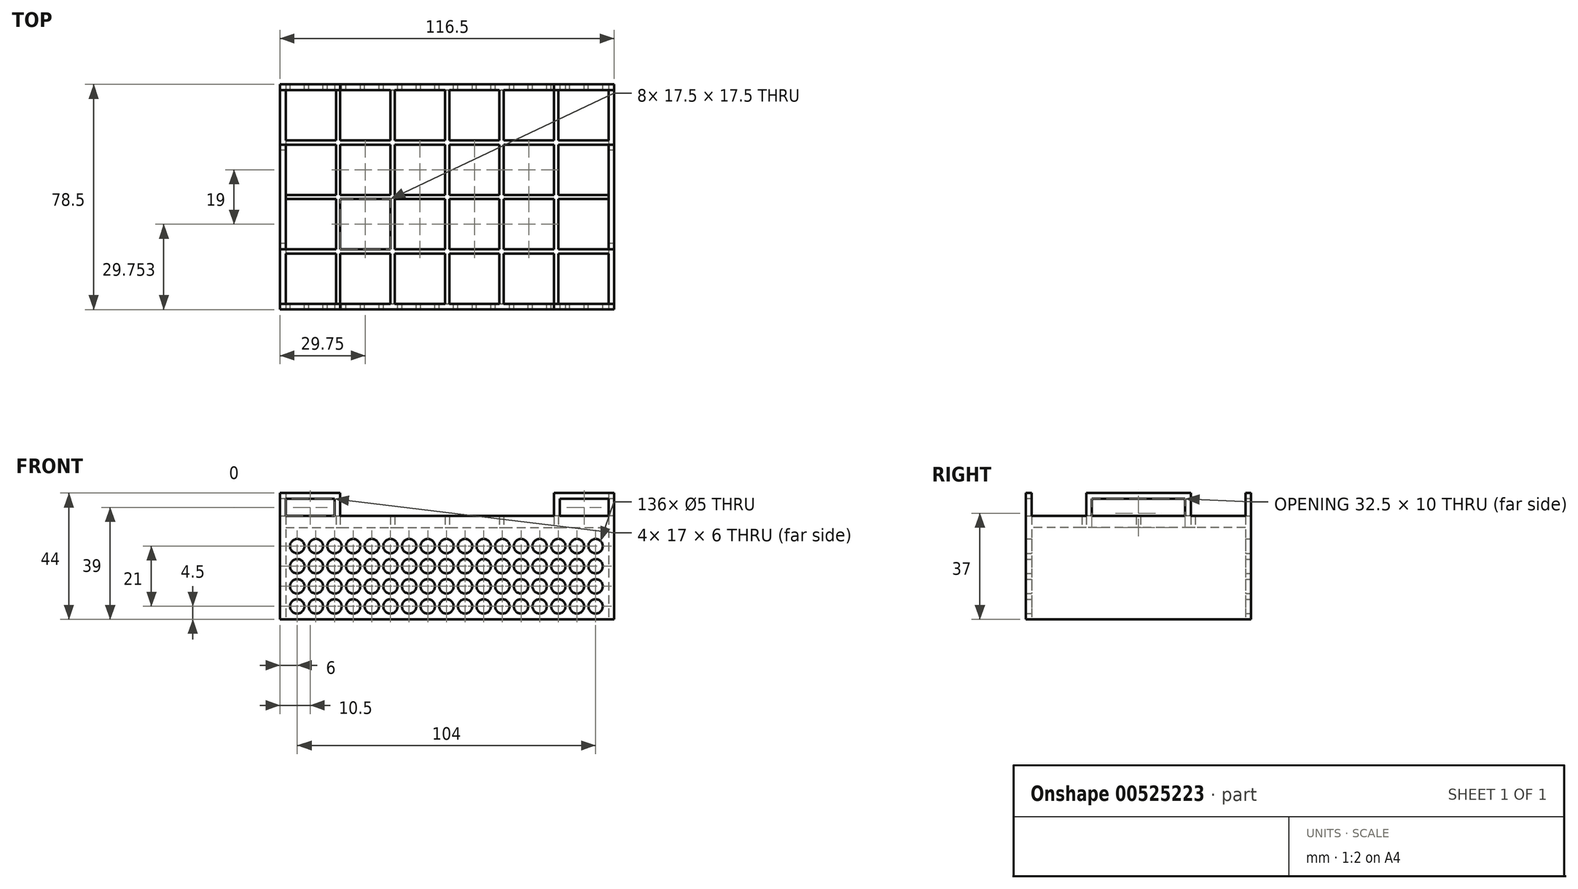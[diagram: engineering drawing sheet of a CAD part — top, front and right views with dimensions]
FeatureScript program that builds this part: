
annotation { "Feature Type Name" : "Feature", "Feature Type Description" : "" }
export const myFeature = defineFeature(function(context is Context, id is Id, definition is map)
    precondition{}
    {
        {
            var Q0;
            Q0=qCreatedBy(makeId("Top.planeOp"),FACE);
            var sketch = newSketch(context, id + "F0", { "sketchPlane" : qUnion([Q0])});
            skLineSegment(sketch, "E0.bottom", {"start": v(-60.16, 39.34) * mm, "end": v(-42.66, 39.34) * mm});
            skLineSegment(sketch, "E0.top", {"start": v(-60.16, 21.84) * mm, "end": v(-42.66, 21.84) * mm});
            skLineSegment(sketch, "E0.left", {"start": v(-60.16, 39.34) * mm, "end": v(-60.16, 21.84) * mm});
            skLineSegment(sketch, "E0.right", {"start": v(-42.66, 39.34) * mm, "end": v(-42.66, 21.84) * mm});
            skLineSegment(sketch, "E1.0.1.0", {"start": v(-42.66, 20.34) * mm, "end": v(-42.66, 2.84) * mm});
            skLineSegment(sketch, "E1.0.1.1", {"start": v(-60.16, 20.34) * mm, "end": v(-42.66, 20.34) * mm});
            skLineSegment(sketch, "E1.0.1.2", {"start": v(-60.16, 20.34) * mm, "end": v(-60.16, 2.84) * mm});
            skLineSegment(sketch, "E1.0.1.3", {"start": v(-60.16, 2.84) * mm, "end": v(-42.66, 2.84) * mm});
            skLineSegment(sketch, "E1.0.2.0", {"start": v(-42.66, 1.34) * mm, "end": v(-42.66, -16.16) * mm});
            skLineSegment(sketch, "E1.0.2.1", {"start": v(-60.16, 1.34) * mm, "end": v(-42.66, 1.34) * mm});
            skLineSegment(sketch, "E1.0.2.2", {"start": v(-60.16, 1.34) * mm, "end": v(-60.16, -16.16) * mm});
            skLineSegment(sketch, "E1.0.2.3", {"start": v(-60.16, -16.16) * mm, "end": v(-42.66, -16.16) * mm});
            skLineSegment(sketch, "E1.0.3.0", {"start": v(-42.66, -17.66) * mm, "end": v(-42.66, -35.16) * mm});
            skLineSegment(sketch, "E1.0.3.1", {"start": v(-60.16, -17.66) * mm, "end": v(-42.66, -17.66) * mm});
            skLineSegment(sketch, "E1.0.3.2", {"start": v(-60.16, -17.66) * mm, "end": v(-60.16, -35.16) * mm});
            skLineSegment(sketch, "E1.0.3.3", {"start": v(-60.16, -35.16) * mm, "end": v(-42.66, -35.16) * mm});
            skLineSegment(sketch, "E1.1.0.0", {"start": v(-23.66, 39.34) * mm, "end": v(-23.66, 21.84) * mm});
            skLineSegment(sketch, "E1.1.0.1", {"start": v(-41.16, 39.34) * mm, "end": v(-23.66, 39.34) * mm});
            skLineSegment(sketch, "E1.1.0.2", {"start": v(-41.16, 39.34) * mm, "end": v(-41.16, 21.84) * mm});
            skLineSegment(sketch, "E1.1.0.3", {"start": v(-41.16, 21.84) * mm, "end": v(-23.66, 21.84) * mm});
            skLineSegment(sketch, "E1.1.1.0", {"start": v(-23.66, 20.34) * mm, "end": v(-23.66, 2.84) * mm});
            skLineSegment(sketch, "E1.1.1.1", {"start": v(-41.16, 20.34) * mm, "end": v(-23.66, 20.34) * mm});
            skLineSegment(sketch, "E1.1.1.2", {"start": v(-41.16, 20.34) * mm, "end": v(-41.16, 2.84) * mm});
            skLineSegment(sketch, "E1.1.1.3", {"start": v(-41.16, 2.84) * mm, "end": v(-23.66, 2.84) * mm});
            skLineSegment(sketch, "E1.1.2.0", {"start": v(-23.66, 1.34) * mm, "end": v(-23.66, -16.16) * mm});
            skLineSegment(sketch, "E1.1.2.1", {"start": v(-41.16, 1.34) * mm, "end": v(-23.66, 1.34) * mm});
            skLineSegment(sketch, "E1.1.2.2", {"start": v(-41.16, 1.34) * mm, "end": v(-41.16, -16.16) * mm});
            skLineSegment(sketch, "E1.1.2.3", {"start": v(-41.16, -16.16) * mm, "end": v(-23.66, -16.16) * mm});
            skLineSegment(sketch, "E1.1.3.0", {"start": v(-23.66, -17.66) * mm, "end": v(-23.66, -35.16) * mm});
            skLineSegment(sketch, "E1.1.3.1", {"start": v(-41.16, -17.66) * mm, "end": v(-23.66, -17.66) * mm});
            skLineSegment(sketch, "E1.1.3.2", {"start": v(-41.16, -17.66) * mm, "end": v(-41.16, -35.16) * mm});
            skLineSegment(sketch, "E1.1.3.3", {"start": v(-41.16, -35.16) * mm, "end": v(-23.66, -35.16) * mm});
            skLineSegment(sketch, "E1.2.0.0", {"start": v(-4.66, 39.34) * mm, "end": v(-4.66, 21.84) * mm});
            skLineSegment(sketch, "E1.2.0.1", {"start": v(-22.16, 39.34) * mm, "end": v(-4.66, 39.34) * mm});
            skLineSegment(sketch, "E1.2.0.2", {"start": v(-22.16, 39.34) * mm, "end": v(-22.16, 21.84) * mm});
            skLineSegment(sketch, "E1.2.0.3", {"start": v(-22.16, 21.84) * mm, "end": v(-4.66, 21.84) * mm});
            skLineSegment(sketch, "E1.2.1.0", {"start": v(-4.66, 20.34) * mm, "end": v(-4.66, 2.84) * mm});
            skLineSegment(sketch, "E1.2.1.1", {"start": v(-22.16, 20.34) * mm, "end": v(-4.66, 20.34) * mm});
            skLineSegment(sketch, "E1.2.1.2", {"start": v(-22.16, 20.34) * mm, "end": v(-22.16, 2.84) * mm});
            skLineSegment(sketch, "E1.2.1.3", {"start": v(-22.16, 2.84) * mm, "end": v(-4.66, 2.84) * mm});
            skLineSegment(sketch, "E1.2.2.0", {"start": v(-4.66, 1.34) * mm, "end": v(-4.66, -16.16) * mm});
            skLineSegment(sketch, "E1.2.2.1", {"start": v(-22.16, 1.34) * mm, "end": v(-4.66, 1.34) * mm});
            skLineSegment(sketch, "E1.2.2.2", {"start": v(-22.16, 1.34) * mm, "end": v(-22.16, -16.16) * mm});
            skLineSegment(sketch, "E1.2.2.3", {"start": v(-22.16, -16.16) * mm, "end": v(-4.66, -16.16) * mm});
            skLineSegment(sketch, "E1.2.3.0", {"start": v(-4.66, -17.66) * mm, "end": v(-4.66, -35.16) * mm});
            skLineSegment(sketch, "E1.2.3.1", {"start": v(-22.16, -17.66) * mm, "end": v(-4.66, -17.66) * mm});
            skLineSegment(sketch, "E1.2.3.2", {"start": v(-22.16, -17.66) * mm, "end": v(-22.16, -35.16) * mm});
            skLineSegment(sketch, "E1.2.3.3", {"start": v(-22.16, -35.16) * mm, "end": v(-4.66, -35.16) * mm});
            skLineSegment(sketch, "E1.3.0.0", {"start": v(14.34, 39.34) * mm, "end": v(14.34, 21.84) * mm});
            skLineSegment(sketch, "E1.3.0.1", {"start": v(-3.16, 39.34) * mm, "end": v(14.34, 39.34) * mm});
            skLineSegment(sketch, "E1.3.0.2", {"start": v(-3.16, 39.34) * mm, "end": v(-3.16, 21.84) * mm});
            skLineSegment(sketch, "E1.3.0.3", {"start": v(-3.16, 21.84) * mm, "end": v(14.34, 21.84) * mm});
            skLineSegment(sketch, "E1.3.1.0", {"start": v(14.34, 20.34) * mm, "end": v(14.34, 2.84) * mm});
            skLineSegment(sketch, "E1.3.1.1", {"start": v(-3.16, 20.34) * mm, "end": v(14.34, 20.34) * mm});
            skLineSegment(sketch, "E1.3.1.2", {"start": v(-3.16, 20.34) * mm, "end": v(-3.16, 2.84) * mm});
            skLineSegment(sketch, "E1.3.1.3", {"start": v(-3.16, 2.84) * mm, "end": v(14.34, 2.84) * mm});
            skLineSegment(sketch, "E1.3.2.0", {"start": v(14.34, 1.34) * mm, "end": v(14.34, -16.16) * mm});
            skLineSegment(sketch, "E1.3.2.1", {"start": v(-3.16, 1.34) * mm, "end": v(14.34, 1.34) * mm});
            skLineSegment(sketch, "E1.3.2.2", {"start": v(-3.16, 1.34) * mm, "end": v(-3.16, -16.16) * mm});
            skLineSegment(sketch, "E1.3.2.3", {"start": v(-3.16, -16.16) * mm, "end": v(14.34, -16.16) * mm});
            skLineSegment(sketch, "E1.3.3.0", {"start": v(14.34, -17.66) * mm, "end": v(14.34, -35.16) * mm});
            skLineSegment(sketch, "E1.3.3.1", {"start": v(-3.16, -17.66) * mm, "end": v(14.34, -17.66) * mm});
            skLineSegment(sketch, "E1.3.3.2", {"start": v(-3.16, -17.66) * mm, "end": v(-3.16, -35.16) * mm});
            skLineSegment(sketch, "E1.3.3.3", {"start": v(-3.16, -35.16) * mm, "end": v(14.34, -35.16) * mm});
            skLineSegment(sketch, "E1.4.0.0", {"start": v(33.34, 39.34) * mm, "end": v(33.34, 21.84) * mm});
            skLineSegment(sketch, "E1.4.0.1", {"start": v(15.84, 39.34) * mm, "end": v(33.34, 39.34) * mm});
            skLineSegment(sketch, "E1.4.0.2", {"start": v(15.84, 39.34) * mm, "end": v(15.84, 21.84) * mm});
            skLineSegment(sketch, "E1.4.0.3", {"start": v(15.84, 21.84) * mm, "end": v(33.34, 21.84) * mm});
            skLineSegment(sketch, "E1.4.1.0", {"start": v(33.34, 20.34) * mm, "end": v(33.34, 2.84) * mm});
            skLineSegment(sketch, "E1.4.1.1", {"start": v(15.84, 20.34) * mm, "end": v(33.34, 20.34) * mm});
            skLineSegment(sketch, "E1.4.1.2", {"start": v(15.84, 20.34) * mm, "end": v(15.84, 2.84) * mm});
            skLineSegment(sketch, "E1.4.1.3", {"start": v(15.84, 2.84) * mm, "end": v(33.34, 2.84) * mm});
            skLineSegment(sketch, "E1.4.2.0", {"start": v(33.34, 1.34) * mm, "end": v(33.34, -16.16) * mm});
            skLineSegment(sketch, "E1.4.2.1", {"start": v(15.84, 1.34) * mm, "end": v(33.34, 1.34) * mm});
            skLineSegment(sketch, "E1.4.2.2", {"start": v(15.84, 1.34) * mm, "end": v(15.84, -16.16) * mm});
            skLineSegment(sketch, "E1.4.2.3", {"start": v(15.84, -16.16) * mm, "end": v(33.34, -16.16) * mm});
            skLineSegment(sketch, "E1.4.3.0", {"start": v(33.34, -17.66) * mm, "end": v(33.34, -35.16) * mm});
            skLineSegment(sketch, "E1.4.3.1", {"start": v(15.84, -17.66) * mm, "end": v(33.34, -17.66) * mm});
            skLineSegment(sketch, "E1.4.3.2", {"start": v(15.84, -17.66) * mm, "end": v(15.84, -35.16) * mm});
            skLineSegment(sketch, "E1.4.3.3", {"start": v(15.84, -35.16) * mm, "end": v(33.34, -35.16) * mm});
            skLineSegment(sketch, "E1.5.0.0", {"start": v(52.34, 39.34) * mm, "end": v(52.34, 21.84) * mm});
            skLineSegment(sketch, "E1.5.0.1", {"start": v(34.84, 39.34) * mm, "end": v(52.34, 39.34) * mm});
            skLineSegment(sketch, "E1.5.0.2", {"start": v(34.84, 39.34) * mm, "end": v(34.84, 21.84) * mm});
            skLineSegment(sketch, "E1.5.0.3", {"start": v(34.84, 21.84) * mm, "end": v(52.34, 21.84) * mm});
            skLineSegment(sketch, "E1.5.1.0", {"start": v(52.34, 20.34) * mm, "end": v(52.34, 2.84) * mm});
            skLineSegment(sketch, "E1.5.1.1", {"start": v(34.84, 20.34) * mm, "end": v(52.34, 20.34) * mm});
            skLineSegment(sketch, "E1.5.1.2", {"start": v(34.84, 20.34) * mm, "end": v(34.84, 2.84) * mm});
            skLineSegment(sketch, "E1.5.1.3", {"start": v(34.84, 2.84) * mm, "end": v(52.34, 2.84) * mm});
            skLineSegment(sketch, "E1.5.2.0", {"start": v(52.34, 1.34) * mm, "end": v(52.34, -16.16) * mm});
            skLineSegment(sketch, "E1.5.2.1", {"start": v(34.84, 1.34) * mm, "end": v(52.34, 1.34) * mm});
            skLineSegment(sketch, "E1.5.2.2", {"start": v(34.84, 1.34) * mm, "end": v(34.84, -16.16) * mm});
            skLineSegment(sketch, "E1.5.2.3", {"start": v(34.84, -16.16) * mm, "end": v(52.34, -16.16) * mm});
            skLineSegment(sketch, "E1.5.3.0", {"start": v(52.34, -17.66) * mm, "end": v(52.34, -35.16) * mm});
            skLineSegment(sketch, "E1.5.3.1", {"start": v(34.84, -17.66) * mm, "end": v(52.34, -17.66) * mm});
            skLineSegment(sketch, "E1.5.3.2", {"start": v(34.84, -17.66) * mm, "end": v(34.84, -35.16) * mm});
            skLineSegment(sketch, "E1.5.3.3", {"start": v(34.84, -35.16) * mm, "end": v(52.34, -35.16) * mm});
            skLineSegment(sketch, "E1.direction1", {"start": v(-42.66, 21.84) * mm, "end": v(-23.66, 21.84) * mm, "construction": true});
            skLineSegment(sketch, "E1.direction2", {"start": v(-42.66, 21.84) * mm, "end": v(-42.66, 2.84) * mm, "construction": true});
            skLineSegment(sketch, "E2.bottom", {"start": v(-62.16, 41.34) * mm, "end": v(54.34, 41.34) * mm});
            skLineSegment(sketch, "E2.top", {"start": v(-62.16, -37.16) * mm, "end": v(54.34, -37.16) * mm});
            skLineSegment(sketch, "E2.left", {"start": v(-62.16, 41.34) * mm, "end": v(-62.16, -37.16) * mm});
            skLineSegment(sketch, "E2.right", {"start": v(54.34, 41.34) * mm, "end": v(54.34, -37.16) * mm});
            skSolve(sketch);
        }
        {
            var Q0;
            Q0 = qSketchRegion(id + "F0", true);
            extrude(context, id + "F1", {"entities" : qUnion([Q0]), "depth" : 4 * mm, "offsetDistance" : 25 * mm});
        }
        {
            var Q0;
            Q0=makeQuery(id+"F1.opExtrude","CAP_FACE",FACE,{"disambiguationData":[OSD([sQuery(id+"F0.wireOp",EDGE,"E0.bottom"),sQuery(id+"F0.wireOp",EDGE,"E0.top"),sQuery(id+"F0.wireOp",EDGE,"E0.left"),sQuery(id+"F0.wireOp",EDGE,"E0.right"),sQuery(id+"F0.wireOp",EDGE,"E1.0.1.0"),sQuery(id+"F0.wireOp",EDGE,"E1.0.1.1"),sQuery(id+"F0.wireOp",EDGE,"E1.0.1.2"),sQuery(id+"F0.wireOp",EDGE,"E1.0.1.3"),sQuery(id+"F0.wireOp",EDGE,"E1.0.2.0"),sQuery(id+"F0.wireOp",EDGE,"E1.0.2.1"),sQuery(id+"F0.wireOp",EDGE,"E1.0.2.2"),sQuery(id+"F0.wireOp",EDGE,"E1.0.2.3"),sQuery(id+"F0.wireOp",EDGE,"E1.0.3.0"),sQuery(id+"F0.wireOp",EDGE,"E1.0.3.1"),sQuery(id+"F0.wireOp",EDGE,"E1.0.3.2"),sQuery(id+"F0.wireOp",EDGE,"E1.0.3.3"),sQuery(id+"F0.wireOp",EDGE,"E1.1.0.0"),sQuery(id+"F0.wireOp",EDGE,"E1.1.0.1"),sQuery(id+"F0.wireOp",EDGE,"E1.1.0.2"),sQuery(id+"F0.wireOp",EDGE,"E1.1.0.3"),sQuery(id+"F0.wireOp",EDGE,"E1.1.1.0"),sQuery(id+"F0.wireOp",EDGE,"E1.1.1.1"),sQuery(id+"F0.wireOp",EDGE,"E1.1.1.2"),sQuery(id+"F0.wireOp",EDGE,"E1.1.1.3"),sQuery(id+"F0.wireOp",EDGE,"E1.1.2.0"),sQuery(id+"F0.wireOp",EDGE,"E1.1.2.1"),sQuery(id+"F0.wireOp",EDGE,"E1.1.2.2"),sQuery(id+"F0.wireOp",EDGE,"E1.1.2.3"),sQuery(id+"F0.wireOp",EDGE,"E1.1.3.0"),sQuery(id+"F0.wireOp",EDGE,"E1.1.3.1"),sQuery(id+"F0.wireOp",EDGE,"E1.1.3.2"),sQuery(id+"F0.wireOp",EDGE,"E1.1.3.3"),sQuery(id+"F0.wireOp",EDGE,"E1.2.0.0"),sQuery(id+"F0.wireOp",EDGE,"E1.2.0.1"),sQuery(id+"F0.wireOp",EDGE,"E1.2.0.2"),sQuery(id+"F0.wireOp",EDGE,"E1.2.0.3"),sQuery(id+"F0.wireOp",EDGE,"E1.2.1.0"),sQuery(id+"F0.wireOp",EDGE,"E1.2.1.1"),sQuery(id+"F0.wireOp",EDGE,"E1.2.1.2"),sQuery(id+"F0.wireOp",EDGE,"E1.2.1.3"),sQuery(id+"F0.wireOp",EDGE,"E1.2.2.0"),sQuery(id+"F0.wireOp",EDGE,"E1.2.2.1"),sQuery(id+"F0.wireOp",EDGE,"E1.2.2.2"),sQuery(id+"F0.wireOp",EDGE,"E1.2.2.3"),sQuery(id+"F0.wireOp",EDGE,"E1.2.3.0"),sQuery(id+"F0.wireOp",EDGE,"E1.2.3.1"),sQuery(id+"F0.wireOp",EDGE,"E1.2.3.2"),sQuery(id+"F0.wireOp",EDGE,"E1.2.3.3"),sQuery(id+"F0.wireOp",EDGE,"E1.3.0.0"),sQuery(id+"F0.wireOp",EDGE,"E1.3.0.1"),sQuery(id+"F0.wireOp",EDGE,"E1.3.0.2"),sQuery(id+"F0.wireOp",EDGE,"E1.3.0.3"),sQuery(id+"F0.wireOp",EDGE,"E1.3.1.0"),sQuery(id+"F0.wireOp",EDGE,"E1.3.1.1"),sQuery(id+"F0.wireOp",EDGE,"E1.3.1.2"),sQuery(id+"F0.wireOp",EDGE,"E1.3.1.3"),sQuery(id+"F0.wireOp",EDGE,"E1.3.2.0"),sQuery(id+"F0.wireOp",EDGE,"E1.3.2.1"),sQuery(id+"F0.wireOp",EDGE,"E1.3.2.2"),sQuery(id+"F0.wireOp",EDGE,"E1.3.2.3"),sQuery(id+"F0.wireOp",EDGE,"E1.3.3.0"),sQuery(id+"F0.wireOp",EDGE,"E1.3.3.1"),sQuery(id+"F0.wireOp",EDGE,"E1.3.3.2"),sQuery(id+"F0.wireOp",EDGE,"E1.3.3.3"),sQuery(id+"F0.wireOp",EDGE,"E1.4.0.0"),sQuery(id+"F0.wireOp",EDGE,"E1.4.0.1"),sQuery(id+"F0.wireOp",EDGE,"E1.4.0.2"),sQuery(id+"F0.wireOp",EDGE,"E1.4.0.3"),sQuery(id+"F0.wireOp",EDGE,"E1.4.1.0"),sQuery(id+"F0.wireOp",EDGE,"E1.4.1.1"),sQuery(id+"F0.wireOp",EDGE,"E1.4.1.2"),sQuery(id+"F0.wireOp",EDGE,"E1.4.1.3"),sQuery(id+"F0.wireOp",EDGE,"E1.4.2.0"),sQuery(id+"F0.wireOp",EDGE,"E1.4.2.1"),sQuery(id+"F0.wireOp",EDGE,"E1.4.2.2"),sQuery(id+"F0.wireOp",EDGE,"E1.4.2.3"),sQuery(id+"F0.wireOp",EDGE,"E1.4.3.0"),sQuery(id+"F0.wireOp",EDGE,"E1.4.3.1"),sQuery(id+"F0.wireOp",EDGE,"E1.4.3.2"),sQuery(id+"F0.wireOp",EDGE,"E1.4.3.3"),sQuery(id+"F0.wireOp",EDGE,"E1.5.0.0"),sQuery(id+"F0.wireOp",EDGE,"E1.5.0.1"),sQuery(id+"F0.wireOp",EDGE,"E1.5.0.2"),sQuery(id+"F0.wireOp",EDGE,"E1.5.0.3"),sQuery(id+"F0.wireOp",EDGE,"E1.5.1.0"),sQuery(id+"F0.wireOp",EDGE,"E1.5.1.1"),sQuery(id+"F0.wireOp",EDGE,"E1.5.1.2"),sQuery(id+"F0.wireOp",EDGE,"E1.5.1.3"),sQuery(id+"F0.wireOp",EDGE,"E1.5.2.0"),sQuery(id+"F0.wireOp",EDGE,"E1.5.2.1"),sQuery(id+"F0.wireOp",EDGE,"E1.5.2.2"),sQuery(id+"F0.wireOp",EDGE,"E1.5.2.3"),sQuery(id+"F0.wireOp",EDGE,"E1.5.3.0"),sQuery(id+"F0.wireOp",EDGE,"E1.5.3.1"),sQuery(id+"F0.wireOp",EDGE,"E1.5.3.2"),sQuery(id+"F0.wireOp",EDGE,"E1.5.3.3"),sQuery(id+"F0.wireOp",EDGE,"E2.bottom"),sQuery(id+"F0.wireOp",EDGE,"E2.top"),sQuery(id+"F0.wireOp",EDGE,"E2.left"),sQuery(id+"F0.wireOp",EDGE,"E2.right")])],"isStart":false});
            var sketch = newSketch(context, id + "F2", { "sketchPlane" : qUnion([Q0])});
            skLineSegment(sketch, "E3.bottom", {"start": v(-62.16, 41.34) * mm, "end": v(-41.16, 41.34) * mm});
            skLineSegment(sketch, "E3.top", {"start": v(-62.16, 39.34) * mm, "end": v(-41.16, 39.34) * mm});
            skLineSegment(sketch, "E3.left", {"start": v(-62.16, 41.34) * mm, "end": v(-62.16, 39.34) * mm});
            skLineSegment(sketch, "E3.right", {"start": v(-41.16, 41.34) * mm, "end": v(-41.16, 39.34) * mm});
            skLineSegment(sketch, "E4.bottom", {"start": v(-62.16, -37.16) * mm, "end": v(-41.16, -37.16) * mm});
            skLineSegment(sketch, "E4.top", {"start": v(-62.16, -35.16) * mm, "end": v(-41.16, -35.16) * mm});
            skLineSegment(sketch, "E4.left", {"start": v(-62.16, -37.16) * mm, "end": v(-62.16, -35.16) * mm});
            skLineSegment(sketch, "E4.right", {"start": v(-41.16, -37.16) * mm, "end": v(-41.16, -35.16) * mm});
            skLineSegment(sketch, "E5.bottom", {"start": v(52.34, 20.34) * mm, "end": v(54.34, 20.34) * mm});
            skLineSegment(sketch, "E5.top", {"start": v(52.34, -16.16) * mm, "end": v(54.34, -16.16) * mm});
            skLineSegment(sketch, "E5.left", {"start": v(52.34, 20.34) * mm, "end": v(52.34, -16.16) * mm});
            skLineSegment(sketch, "E5.right", {"start": v(54.34, 20.34) * mm, "end": v(54.34, -16.16) * mm});
            skLineSegment(sketch, "E6.bottom", {"start": v(-60.16, 20.34) * mm, "end": v(-62.16, 20.34) * mm});
            skLineSegment(sketch, "E6.top", {"start": v(-60.16, -16.16) * mm, "end": v(-62.16, -16.16) * mm});
            skLineSegment(sketch, "E6.left", {"start": v(-60.16, 20.34) * mm, "end": v(-60.16, -16.16) * mm});
            skLineSegment(sketch, "E6.right", {"start": v(-62.16, 20.34) * mm, "end": v(-62.16, -16.16) * mm});
            skLineSegment(sketch, "E7.bottom", {"start": v(54.34, -37.16) * mm, "end": v(33.34, -37.16) * mm});
            skLineSegment(sketch, "E7.top", {"start": v(54.34, -35.16) * mm, "end": v(33.34, -35.16) * mm});
            skLineSegment(sketch, "E7.left", {"start": v(54.34, -37.16) * mm, "end": v(54.34, -35.16) * mm});
            skLineSegment(sketch, "E7.right", {"start": v(33.34, -37.16) * mm, "end": v(33.34, -35.16) * mm});
            skLineSegment(sketch, "E8.bottom", {"start": v(33.34, 39.34) * mm, "end": v(54.34, 39.34) * mm});
            skLineSegment(sketch, "E8.top", {"start": v(33.34, 41.34) * mm, "end": v(54.34, 41.34) * mm});
            skLineSegment(sketch, "E8.left", {"start": v(33.34, 39.34) * mm, "end": v(33.34, 41.34) * mm});
            skLineSegment(sketch, "E8.right", {"start": v(54.34, 39.34) * mm, "end": v(54.34, 41.34) * mm});
            skSolve(sketch);
        }
        {
            var Q0;
            Q0 = qSketchRegion(id + "F2", true);
            extrude(context, id + "F3", {"entities" : qUnion([Q0]), "operationType" : NewBodyOperationType.ADD, "depth" : 8 * mm, "offsetDistance" : 25 * mm});
        }
        {
            var Q0;
            Q0=makeQuery(id+"F3.boolean.opBoolean","MERGE",FACE,{"derivedFrom":[makeQuery(id+"F1.opExtrude","SWEPT_FACE",FACE,{"disambiguationData":[OSD([sQuery(id+"F0.wireOp",EDGE,"E2.left")])]}),makeQuery(id+"F3.opExtrude","SWEPT_FACE",FACE,{"disambiguationData":[OSD([sQuery(id+"F2.wireOp",EDGE,"E3.left")])]}),makeQuery(id+"F3.opExtrude","SWEPT_FACE",FACE,{"disambiguationData":[OSD([sQuery(id+"F2.wireOp",EDGE,"E4.left")])]}),makeQuery(id+"F3.opExtrude","SWEPT_FACE",FACE,{"disambiguationData":[OSD([sQuery(id+"F2.wireOp",EDGE,"E6.right")])]})]});
            var sketch = newSketch(context, id + "F4", { "sketchPlane" : qUnion([Q0])});
            skLineSegment(sketch, "E9.bottom", {"start": v(-18.34, 10) * mm, "end": v(14.16, 10) * mm});
            skLineSegment(sketch, "E9.top", {"start": v(-18.34, 4) * mm, "end": v(14.16, 4) * mm});
            skLineSegment(sketch, "E9.left", {"start": v(-18.34, 10) * mm, "end": v(-18.34, 4) * mm});
            skLineSegment(sketch, "E9.right", {"start": v(14.16, 10) * mm, "end": v(14.16, 4) * mm});
            skSolve(sketch);
        }
        {
            var Q0;
            Q0 = qSketchRegion(id + "F4", true);
            extrude(context, id + "F5", {"entities" : qUnion([Q0]), "operationType" : NewBodyOperationType.REMOVE, "endBound" : BoundingType.THROUGH_ALL, "oppositeDirection" : true, "depth" : 25 * mm, "offsetDistance" : 25 * mm});
        }
        {
            var Q0;
            Q0=makeQuery(id+"F3.boolean.opBoolean","MERGE",FACE,{"derivedFrom":[makeQuery(id+"F1.opExtrude","SWEPT_FACE",FACE,{"disambiguationData":[OSD([sQuery(id+"F0.wireOp",EDGE,"E2.top")])]}),makeQuery(id+"F3.opExtrude","SWEPT_FACE",FACE,{"disambiguationData":[OSD([sQuery(id+"F2.wireOp",EDGE,"E4.bottom")])]}),makeQuery(id+"F3.opExtrude","SWEPT_FACE",FACE,{"disambiguationData":[OSD([sQuery(id+"F2.wireOp",EDGE,"9MrdIHgc-yS0F-vLJ0-OXnb-LXY7ecxZvSkL.bottom")])]})]});
            var sketch = newSketch(context, id + "F6", { "sketchPlane" : qUnion([Q0])});
            skLineSegment(sketch, "E10.bottom", {"start": v(-60.16, 10) * mm, "end": v(-43.16, 10) * mm});
            skLineSegment(sketch, "E10.top", {"start": v(-60.16, 4) * mm, "end": v(-43.16, 4) * mm});
            skLineSegment(sketch, "E10.left", {"start": v(-60.16, 10) * mm, "end": v(-60.16, 4) * mm});
            skLineSegment(sketch, "E10.right", {"start": v(-43.16, 10) * mm, "end": v(-43.16, 4) * mm});
            skLineSegment(sketch, "E11.MirrorCS", {"start": v(52.34, 10) * mm, "end": v(35.34, 10) * mm});
            skLineSegment(sketch, "E12.MirrorCS", {"start": v(35.34, 4) * mm, "end": v(35.34, 10) * mm});
            skLineSegment(sketch, "E13.MirrorCS", {"start": v(52.34, 4) * mm, "end": v(-43.16, 4) * mm});
            skLineSegment(sketch, "E14", {"start": v(52.34, 10) * mm, "end": v(52.34, 4) * mm});
            skSolve(sketch);
        }
        {
            var Q0;
            Q0 = qSketchRegion(id + "F6", true);
            extrude(context, id + "F7", {"entities" : qUnion([Q0]), "operationType" : NewBodyOperationType.REMOVE, "endBound" : BoundingType.THROUGH_ALL, "oppositeDirection" : true, "depth" : 25 * mm, "offsetDistance" : 25 * mm});
        }
        {
            var Q0;
            Q0=makeQuery(id+"F1.opExtrude","CAP_FACE",FACE,{"disambiguationData":[OSD([sQuery(id+"F0.wireOp",EDGE,"E0.bottom"),sQuery(id+"F0.wireOp",EDGE,"E0.top"),sQuery(id+"F0.wireOp",EDGE,"E0.left"),sQuery(id+"F0.wireOp",EDGE,"E0.right"),sQuery(id+"F0.wireOp",EDGE,"E1.0.1.0"),sQuery(id+"F0.wireOp",EDGE,"E1.0.1.1"),sQuery(id+"F0.wireOp",EDGE,"E1.0.1.2"),sQuery(id+"F0.wireOp",EDGE,"E1.0.1.3"),sQuery(id+"F0.wireOp",EDGE,"E1.0.2.0"),sQuery(id+"F0.wireOp",EDGE,"E1.0.2.1"),sQuery(id+"F0.wireOp",EDGE,"E1.0.2.2"),sQuery(id+"F0.wireOp",EDGE,"E1.0.2.3"),sQuery(id+"F0.wireOp",EDGE,"E1.0.3.0"),sQuery(id+"F0.wireOp",EDGE,"E1.0.3.1"),sQuery(id+"F0.wireOp",EDGE,"E1.0.3.2"),sQuery(id+"F0.wireOp",EDGE,"E1.0.3.3"),sQuery(id+"F0.wireOp",EDGE,"E1.1.0.0"),sQuery(id+"F0.wireOp",EDGE,"E1.1.0.1"),sQuery(id+"F0.wireOp",EDGE,"E1.1.0.2"),sQuery(id+"F0.wireOp",EDGE,"E1.1.0.3"),sQuery(id+"F0.wireOp",EDGE,"E1.1.1.0"),sQuery(id+"F0.wireOp",EDGE,"E1.1.1.1"),sQuery(id+"F0.wireOp",EDGE,"E1.1.1.2"),sQuery(id+"F0.wireOp",EDGE,"E1.1.1.3"),sQuery(id+"F0.wireOp",EDGE,"E1.1.2.0"),sQuery(id+"F0.wireOp",EDGE,"E1.1.2.1"),sQuery(id+"F0.wireOp",EDGE,"E1.1.2.2"),sQuery(id+"F0.wireOp",EDGE,"E1.1.2.3"),sQuery(id+"F0.wireOp",EDGE,"E1.1.3.0"),sQuery(id+"F0.wireOp",EDGE,"E1.1.3.1"),sQuery(id+"F0.wireOp",EDGE,"E1.1.3.2"),sQuery(id+"F0.wireOp",EDGE,"E1.1.3.3"),sQuery(id+"F0.wireOp",EDGE,"E1.2.0.0"),sQuery(id+"F0.wireOp",EDGE,"E1.2.0.1"),sQuery(id+"F0.wireOp",EDGE,"E1.2.0.2"),sQuery(id+"F0.wireOp",EDGE,"E1.2.0.3"),sQuery(id+"F0.wireOp",EDGE,"E1.2.1.0"),sQuery(id+"F0.wireOp",EDGE,"E1.2.1.1"),sQuery(id+"F0.wireOp",EDGE,"E1.2.1.2"),sQuery(id+"F0.wireOp",EDGE,"E1.2.1.3"),sQuery(id+"F0.wireOp",EDGE,"E1.2.2.0"),sQuery(id+"F0.wireOp",EDGE,"E1.2.2.1"),sQuery(id+"F0.wireOp",EDGE,"E1.2.2.2"),sQuery(id+"F0.wireOp",EDGE,"E1.2.2.3"),sQuery(id+"F0.wireOp",EDGE,"E1.2.3.0"),sQuery(id+"F0.wireOp",EDGE,"E1.2.3.1"),sQuery(id+"F0.wireOp",EDGE,"E1.2.3.2"),sQuery(id+"F0.wireOp",EDGE,"E1.2.3.3"),sQuery(id+"F0.wireOp",EDGE,"E1.3.0.0"),sQuery(id+"F0.wireOp",EDGE,"E1.3.0.1"),sQuery(id+"F0.wireOp",EDGE,"E1.3.0.2"),sQuery(id+"F0.wireOp",EDGE,"E1.3.0.3"),sQuery(id+"F0.wireOp",EDGE,"E1.3.1.0"),sQuery(id+"F0.wireOp",EDGE,"E1.3.1.1"),sQuery(id+"F0.wireOp",EDGE,"E1.3.1.2"),sQuery(id+"F0.wireOp",EDGE,"E1.3.1.3"),sQuery(id+"F0.wireOp",EDGE,"E1.3.2.0"),sQuery(id+"F0.wireOp",EDGE,"E1.3.2.1"),sQuery(id+"F0.wireOp",EDGE,"E1.3.2.2"),sQuery(id+"F0.wireOp",EDGE,"E1.3.2.3"),sQuery(id+"F0.wireOp",EDGE,"E1.3.3.0"),sQuery(id+"F0.wireOp",EDGE,"E1.3.3.1"),sQuery(id+"F0.wireOp",EDGE,"E1.3.3.2"),sQuery(id+"F0.wireOp",EDGE,"E1.3.3.3"),sQuery(id+"F0.wireOp",EDGE,"E1.4.0.0"),sQuery(id+"F0.wireOp",EDGE,"E1.4.0.1"),sQuery(id+"F0.wireOp",EDGE,"E1.4.0.2"),sQuery(id+"F0.wireOp",EDGE,"E1.4.0.3"),sQuery(id+"F0.wireOp",EDGE,"E1.4.1.0"),sQuery(id+"F0.wireOp",EDGE,"E1.4.1.1"),sQuery(id+"F0.wireOp",EDGE,"E1.4.1.2"),sQuery(id+"F0.wireOp",EDGE,"E1.4.1.3"),sQuery(id+"F0.wireOp",EDGE,"E1.4.2.0"),sQuery(id+"F0.wireOp",EDGE,"E1.4.2.1"),sQuery(id+"F0.wireOp",EDGE,"E1.4.2.2"),sQuery(id+"F0.wireOp",EDGE,"E1.4.2.3"),sQuery(id+"F0.wireOp",EDGE,"E1.4.3.0"),sQuery(id+"F0.wireOp",EDGE,"E1.4.3.1"),sQuery(id+"F0.wireOp",EDGE,"E1.4.3.2"),sQuery(id+"F0.wireOp",EDGE,"E1.4.3.3"),sQuery(id+"F0.wireOp",EDGE,"E1.5.0.0"),sQuery(id+"F0.wireOp",EDGE,"E1.5.0.1"),sQuery(id+"F0.wireOp",EDGE,"E1.5.0.2"),sQuery(id+"F0.wireOp",EDGE,"E1.5.0.3"),sQuery(id+"F0.wireOp",EDGE,"E1.5.1.0"),sQuery(id+"F0.wireOp",EDGE,"E1.5.1.1"),sQuery(id+"F0.wireOp",EDGE,"E1.5.1.2"),sQuery(id+"F0.wireOp",EDGE,"E1.5.1.3"),sQuery(id+"F0.wireOp",EDGE,"E1.5.2.0"),sQuery(id+"F0.wireOp",EDGE,"E1.5.2.1"),sQuery(id+"F0.wireOp",EDGE,"E1.5.2.2"),sQuery(id+"F0.wireOp",EDGE,"E1.5.2.3"),sQuery(id+"F0.wireOp",EDGE,"E1.5.3.0"),sQuery(id+"F0.wireOp",EDGE,"E1.5.3.1"),sQuery(id+"F0.wireOp",EDGE,"E1.5.3.2"),sQuery(id+"F0.wireOp",EDGE,"E1.5.3.3"),sQuery(id+"F0.wireOp",EDGE,"E2.bottom"),sQuery(id+"F0.wireOp",EDGE,"E2.top"),sQuery(id+"F0.wireOp",EDGE,"E2.left"),sQuery(id+"F0.wireOp",EDGE,"E2.right")])],"isStart":true});
            var sketch = newSketch(context, id + "F8", { "sketchPlane" : qUnion([Q0])});
            skLineSegment(sketch, "E15.bottom", {"start": v(-62.16, 37.16) * mm, "end": v(54.34, 37.16) * mm});
            skLineSegment(sketch, "E15.top", {"start": v(-62.16, -41.34) * mm, "end": v(54.34, -41.34) * mm});
            skLineSegment(sketch, "E15.left", {"start": v(-62.16, 37.16) * mm, "end": v(-62.16, -41.34) * mm});
            skLineSegment(sketch, "E15.right", {"start": v(54.34, 37.16) * mm, "end": v(54.34, -41.34) * mm});
            skLineSegment(sketch, "E16.bottom", {"start": v(-60.16, 35.16) * mm, "end": v(52.34, 35.16) * mm});
            skLineSegment(sketch, "E16.top", {"start": v(-60.16, -39.34) * mm, "end": v(52.34, -39.34) * mm});
            skLineSegment(sketch, "E16.left", {"start": v(-60.16, 35.16) * mm, "end": v(-60.16, -39.34) * mm});
            skLineSegment(sketch, "E16.right", {"start": v(52.34, 35.16) * mm, "end": v(52.34, -39.34) * mm});
            skSolve(sketch);
        }
        {
            var Q0;
            Q0 = qSketchRegion(id + "F8", true);
            extrude(context, id + "F9", {"entities" : qUnion([Q0]), "operationType" : NewBodyOperationType.ADD, "depth" : 32 * mm, "offsetDistance" : 25 * mm});
        }
        {
            var Q0;
            Q0=makeQuery(id+"F9.boolean.opBoolean","MERGE",FACE,{"derivedFrom":[makeQuery(id+"F3.boolean.opBoolean","MERGE",FACE,{"derivedFrom":[makeQuery(id+"F1.opExtrude","SWEPT_FACE",FACE,{"disambiguationData":[OSD([sQuery(id+"F0.wireOp",EDGE,"E2.bottom")])]}),makeQuery(id+"F3.opExtrude","SWEPT_FACE",FACE,{"disambiguationData":[OSD([sQuery(id+"F2.wireOp",EDGE,"E3.bottom")])]}),makeQuery(id+"F3.opExtrude","SWEPT_FACE",FACE,{"disambiguationData":[OSD([sQuery(id+"F2.wireOp",EDGE,"E8.top")])]})]}),makeQuery(id+"F9.opExtrude","SWEPT_FACE",FACE,{"disambiguationData":[OSD([sQuery(id+"F8.wireOp",EDGE,"E15.top")])]})]});
            var sketch = newSketch(context, id + "F10", { "sketchPlane" : qUnion([Q0])});
            skCircle(sketch, "E17", {"center": v(-47.84, -27.5) * mm, "radius": 2.5 * mm});
            skCircle(sketch, "E18.0.1.0", {"center": v(-47.84, -20.5) * mm, "radius": 2.5 * mm});
            skCircle(sketch, "E18.0.2.0", {"center": v(-47.84, -13.5) * mm, "radius": 2.5 * mm});
            skCircle(sketch, "E18.0.3.0", {"center": v(-47.84, -6.5) * mm, "radius": 2.5 * mm});
            skCircle(sketch, "E18.1.0.0", {"center": v(-41.34, -27.5) * mm, "radius": 2.5 * mm});
            skCircle(sketch, "E18.1.1.0", {"center": v(-41.34, -20.5) * mm, "radius": 2.5 * mm});
            skCircle(sketch, "E18.1.2.0", {"center": v(-41.34, -13.5) * mm, "radius": 2.5 * mm});
            skCircle(sketch, "E18.1.3.0", {"center": v(-41.34, -6.5) * mm, "radius": 2.5 * mm});
            skCircle(sketch, "E18.2.0.0", {"center": v(-34.84, -27.5) * mm, "radius": 2.5 * mm});
            skCircle(sketch, "E18.2.1.0", {"center": v(-34.84, -20.5) * mm, "radius": 2.5 * mm});
            skCircle(sketch, "E18.2.2.0", {"center": v(-34.84, -13.5) * mm, "radius": 2.5 * mm});
            skCircle(sketch, "E18.2.3.0", {"center": v(-34.84, -6.5) * mm, "radius": 2.5 * mm});
            skCircle(sketch, "E18.3.0.0", {"center": v(-28.34, -27.5) * mm, "radius": 2.5 * mm});
            skCircle(sketch, "E18.3.1.0", {"center": v(-28.34, -20.5) * mm, "radius": 2.5 * mm});
            skCircle(sketch, "E18.3.2.0", {"center": v(-28.34, -13.5) * mm, "radius": 2.5 * mm});
            skCircle(sketch, "E18.3.3.0", {"center": v(-28.34, -6.5) * mm, "radius": 2.5 * mm});
            skCircle(sketch, "E18.4.0.0", {"center": v(-21.84, -27.5) * mm, "radius": 2.5 * mm});
            skCircle(sketch, "E18.4.1.0", {"center": v(-21.84, -20.5) * mm, "radius": 2.5 * mm});
            skCircle(sketch, "E18.4.2.0", {"center": v(-21.84, -13.5) * mm, "radius": 2.5 * mm});
            skCircle(sketch, "E18.4.3.0", {"center": v(-21.84, -6.5) * mm, "radius": 2.5 * mm});
            skCircle(sketch, "E18.5.0.0", {"center": v(-15.34, -27.5) * mm, "radius": 2.5 * mm});
            skCircle(sketch, "E18.5.1.0", {"center": v(-15.34, -20.5) * mm, "radius": 2.5 * mm});
            skCircle(sketch, "E18.5.2.0", {"center": v(-15.34, -13.5) * mm, "radius": 2.5 * mm});
            skCircle(sketch, "E18.5.3.0", {"center": v(-15.34, -6.5) * mm, "radius": 2.5 * mm});
            skCircle(sketch, "E18.6.0.0", {"center": v(-8.84, -27.5) * mm, "radius": 2.5 * mm});
            skCircle(sketch, "E18.6.1.0", {"center": v(-8.84, -20.5) * mm, "radius": 2.5 * mm});
            skCircle(sketch, "E18.6.2.0", {"center": v(-8.84, -13.5) * mm, "radius": 2.5 * mm});
            skCircle(sketch, "E18.6.3.0", {"center": v(-8.84, -6.5) * mm, "radius": 2.5 * mm});
            skCircle(sketch, "E18.7.0.0", {"center": v(-2.34, -27.5) * mm, "radius": 2.5 * mm});
            skCircle(sketch, "E18.7.1.0", {"center": v(-2.34, -20.5) * mm, "radius": 2.5 * mm});
            skCircle(sketch, "E18.7.2.0", {"center": v(-2.34, -13.5) * mm, "radius": 2.5 * mm});
            skCircle(sketch, "E18.7.3.0", {"center": v(-2.34, -6.5) * mm, "radius": 2.5 * mm});
            skCircle(sketch, "E18.8.0.0", {"center": v(4.16, -27.5) * mm, "radius": 2.5 * mm});
            skCircle(sketch, "E18.8.1.0", {"center": v(4.16, -20.5) * mm, "radius": 2.5 * mm});
            skCircle(sketch, "E18.8.2.0", {"center": v(4.16, -13.5) * mm, "radius": 2.5 * mm});
            skCircle(sketch, "E18.8.3.0", {"center": v(4.16, -6.5) * mm, "radius": 2.5 * mm});
            skCircle(sketch, "E18.9.0.0", {"center": v(10.66, -27.5) * mm, "radius": 2.5 * mm});
            skCircle(sketch, "E18.9.1.0", {"center": v(10.66, -20.5) * mm, "radius": 2.5 * mm});
            skCircle(sketch, "E18.9.2.0", {"center": v(10.66, -13.5) * mm, "radius": 2.5 * mm});
            skCircle(sketch, "E18.9.3.0", {"center": v(10.66, -6.5) * mm, "radius": 2.5 * mm});
            skCircle(sketch, "E18.10.0.0", {"center": v(17.16, -27.5) * mm, "radius": 2.5 * mm});
            skCircle(sketch, "E18.10.1.0", {"center": v(17.16, -20.5) * mm, "radius": 2.5 * mm});
            skCircle(sketch, "E18.10.2.0", {"center": v(17.16, -13.5) * mm, "radius": 2.5 * mm});
            skCircle(sketch, "E18.10.3.0", {"center": v(17.16, -6.5) * mm, "radius": 2.5 * mm});
            skCircle(sketch, "E18.11.0.0", {"center": v(23.66, -27.5) * mm, "radius": 2.5 * mm});
            skCircle(sketch, "E18.11.1.0", {"center": v(23.66, -20.5) * mm, "radius": 2.5 * mm});
            skCircle(sketch, "E18.11.2.0", {"center": v(23.66, -13.5) * mm, "radius": 2.5 * mm});
            skCircle(sketch, "E18.11.3.0", {"center": v(23.66, -6.5) * mm, "radius": 2.5 * mm});
            skCircle(sketch, "E18.12.0.0", {"center": v(30.16, -27.5) * mm, "radius": 2.5 * mm});
            skCircle(sketch, "E18.12.1.0", {"center": v(30.16, -20.5) * mm, "radius": 2.5 * mm});
            skCircle(sketch, "E18.12.2.0", {"center": v(30.16, -13.5) * mm, "radius": 2.5 * mm});
            skCircle(sketch, "E18.12.3.0", {"center": v(30.16, -6.5) * mm, "radius": 2.5 * mm});
            skCircle(sketch, "E18.13.0.0", {"center": v(36.66, -27.5) * mm, "radius": 2.5 * mm});
            skCircle(sketch, "E18.13.1.0", {"center": v(36.66, -20.5) * mm, "radius": 2.5 * mm});
            skCircle(sketch, "E18.13.2.0", {"center": v(36.66, -13.5) * mm, "radius": 2.5 * mm});
            skCircle(sketch, "E18.13.3.0", {"center": v(36.66, -6.5) * mm, "radius": 2.5 * mm});
            skCircle(sketch, "E18.14.0.0", {"center": v(43.16, -27.5) * mm, "radius": 2.5 * mm});
            skCircle(sketch, "E18.14.1.0", {"center": v(43.16, -20.5) * mm, "radius": 2.5 * mm});
            skCircle(sketch, "E18.14.2.0", {"center": v(43.16, -13.5) * mm, "radius": 2.5 * mm});
            skCircle(sketch, "E18.14.3.0", {"center": v(43.16, -6.5) * mm, "radius": 2.5 * mm});
            skCircle(sketch, "E18.15.0.0", {"center": v(49.66, -27.5) * mm, "radius": 2.5 * mm});
            skCircle(sketch, "E18.15.1.0", {"center": v(49.66, -20.5) * mm, "radius": 2.5 * mm});
            skCircle(sketch, "E18.15.2.0", {"center": v(49.66, -13.5) * mm, "radius": 2.5 * mm});
            skCircle(sketch, "E18.15.3.0", {"center": v(49.66, -6.5) * mm, "radius": 2.5 * mm});
            skLineSegment(sketch, "E18.direction1", {"start": v(-47.84, -27.5) * mm, "end": v(-41.34, -27.5) * mm, "construction": true});
            skLineSegment(sketch, "E18.direction2", {"start": v(-47.84, -27.5) * mm, "end": v(-47.84, -20.5) * mm, "construction": true});
            skCircle(sketch, "E19.0.16.0", {"center": v(56.16, -27.5) * mm, "radius": 2.5 * mm});
            skCircle(sketch, "E19.0.16.1", {"center": v(56.16, -20.5) * mm, "radius": 2.5 * mm});
            skCircle(sketch, "E19.0.16.2", {"center": v(56.16, -13.5) * mm, "radius": 2.5 * mm});
            skCircle(sketch, "E19.0.16.3", {"center": v(56.16, -6.5) * mm, "radius": 2.5 * mm});
            skSolve(sketch);
        }
        {
            var Q0;
            Q0 = qSketchRegion(id + "F10", true);
            extrude(context, id + "F11", {"entities" : qUnion([Q0]), "operationType" : NewBodyOperationType.REMOVE, "endBound" : BoundingType.THROUGH_ALL, "oppositeDirection" : true, "depth" : 25 * mm, "offsetDistance" : 25 * mm});
        }
    });
